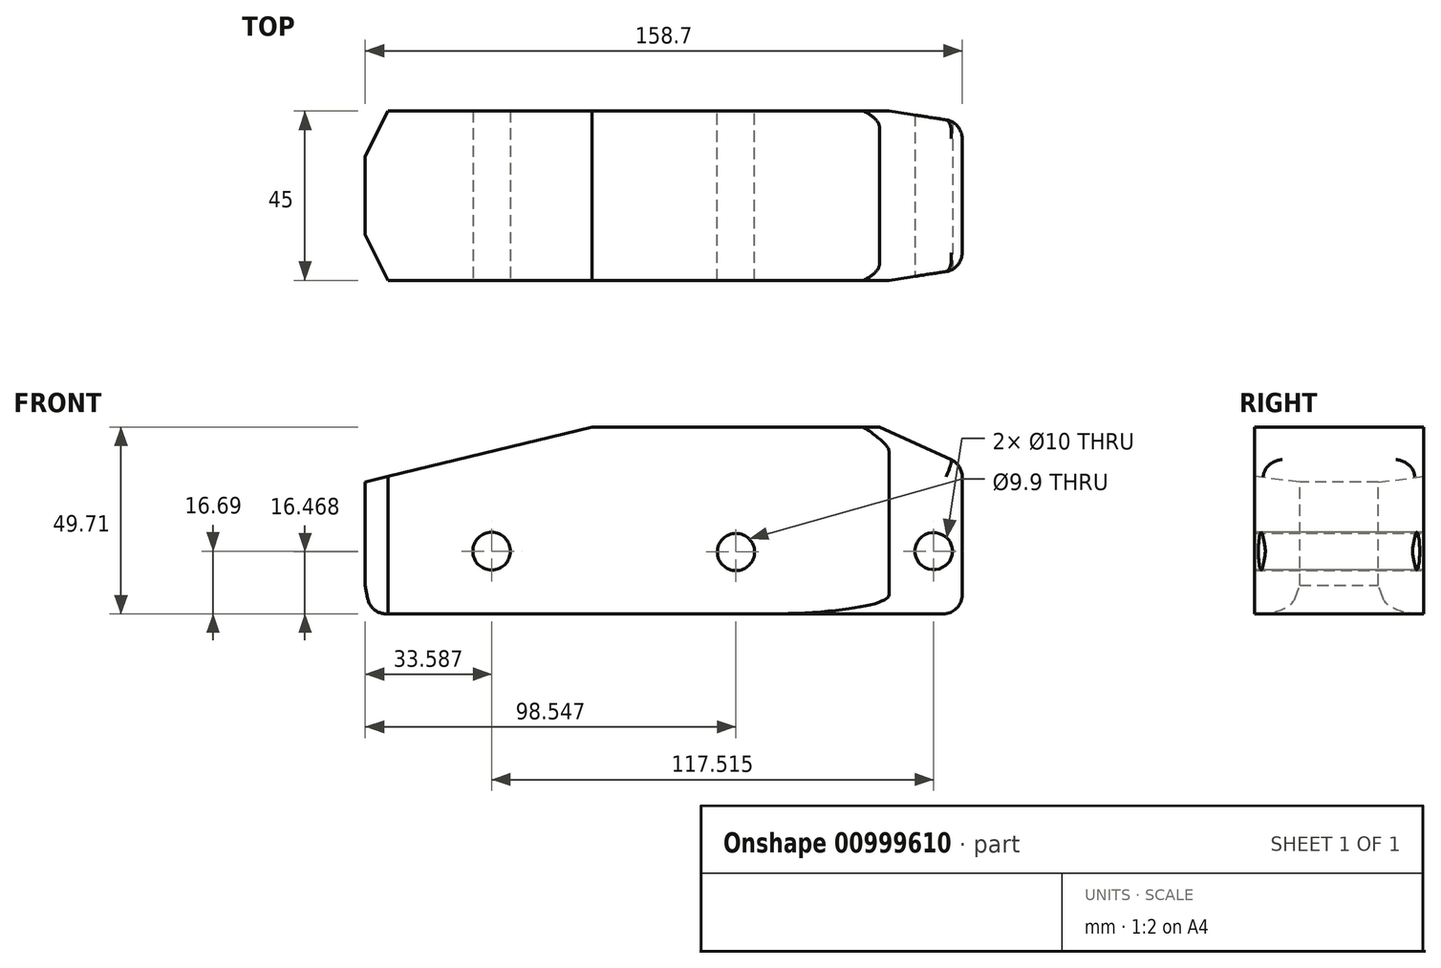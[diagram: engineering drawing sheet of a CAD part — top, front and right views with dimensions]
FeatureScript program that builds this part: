
annotation { "Feature Type Name" : "Feature", "Feature Type Description" : "" }
export const myFeature = defineFeature(function(context is Context, id is Id, definition is map)
    precondition{}
    {
        {
            var Q0;
            Q0=qCreatedBy(makeId("Front.planeOp"),FACE);
            var sketch = newSketch(context, id + "F0", { "sketchPlane" : qUnion([Q0])});
            skLineSegment(sketch, "E0.top", {"start": v(0, -49.7) * mm, "end": v(-135.3, -49.7) * mm});
            skLineSegment(sketch, "E0.left", {"start": v(0, 0) * mm, "end": v(0, -49.7) * mm});
            skLineSegment(sketch, "E1.bottom", {"start": v(0, -49.7) * mm, "end": v(24.63, -49.7) * mm});
            skLineSegment(sketch, "E2", {"start": v(49.26, -22.51) * mm, "end": v(0, 0) * mm});
            skLineSegment(sketch, "E3", {"start": v(24.63, -49.7) * mm, "end": v(49.26, -22.51) * mm});
            skPoint(sketch, "E4.orphan", {"position": v(49.26, -49.7) * mm});
            skLineSegment(sketch, "E5", {"start": v(0, 0) * mm, "end": v(-76.46, 0) * mm});
            skLineSegment(sketch, "E6", {"start": v(-76.46, 0) * mm, "end": v(-141.55, -15.83) * mm});
            skLineSegment(sketch, "E7", {"start": v(-141.55, -15.83) * mm, "end": v(-135.3, -49.7) * mm});
            skSolve(sketch);
        }
        {
            var Q0;
            Q0=makeQuery(id+"F0.imprint","IMPRINT",FACE,{"disambiguationData":[TD([[makeQuery(id+"F0.imprint","IMPRINT",EDGE,{"derivedFrom":sQuery(id+"F0.wireOp",EDGE,"E0.left")}),1.0]])]});
            var Q1;
            Q1=makeQuery(id+"F0.imprint","IMPRINT",FACE,{"disambiguationData":[TD([[makeQuery(id+"F0.imprint","IMPRINT",EDGE,{"derivedFrom":sQuery(id+"F0.wireOp",EDGE,"E0.top")}),-1.0]])]});
            extrude(context, id + "F1", {"entities" : qUnion([Q0, Q1]), "endBound" : BoundingType.SYMMETRIC, "depth" : 45 * mm, "offsetDistance" : 25.4 * mm});
        }
        {
            var Q0;
            Q0=qCreatedBy(makeId("Top.planeOp"),FACE);
            var sketch = newSketch(context, id + "F2", { "sketchPlane" : qUnion([Q0])});
            skLineSegment(sketch, "E8", {"start": v(0, 22.88) * mm, "end": v(24.46, 19.14) * mm});
            skLineSegment(sketch, "E9", {"start": v(24.46, 19.14) * mm, "end": v(42.3, 8.78) * mm});
            skLineSegment(sketch, "E10", {"start": v(42.3, 8.78) * mm, "end": v(46.62, 0) * mm});
            skLineSegment(sketch, "E11.MirrorCS", {"start": v(24.46, -19.14) * mm, "end": v(42.3, -8.78) * mm});
            skLineSegment(sketch, "E12.MirrorCS", {"start": v(0, -22.88) * mm, "end": v(24.46, -19.14) * mm});
            skLineSegment(sketch, "E13.MirrorCS", {"start": v(42.3, -8.78) * mm, "end": v(46.62, 0) * mm});
            skLineSegment(sketch, "E14.bottom", {"start": v(0, 54.83) * mm, "end": v(75.1, 54.83) * mm});
            skLineSegment(sketch, "E14.top", {"start": v(0, -56.55) * mm, "end": v(75.1, -56.55) * mm});
            skLineSegment(sketch, "E14.left", {"start": v(0, 54.83) * mm, "end": v(0, -56.55) * mm});
            skLineSegment(sketch, "E14.right", {"start": v(75.1, 54.83) * mm, "end": v(75.1, -56.55) * mm});
            skLineSegment(sketch, "E15", {"start": v(-130.67, -22.5) * mm, "end": v(-136.72, -10.41) * mm});
            skLineSegment(sketch, "E16", {"start": v(-136.72, -10.41) * mm, "end": v(-136.72, 0) * mm});
            skLineSegment(sketch, "E17.MirrorCS", {"start": v(-130.67, 22.5) * mm, "end": v(-136.72, 10.41) * mm});
            skLineSegment(sketch, "E18.MirrorCS", {"start": v(-136.72, 10.41) * mm, "end": v(-136.72, 0) * mm});
            skLineSegment(sketch, "E19.bottom", {"start": v(-125.78, -39.29) * mm, "end": v(-192.55, -39.29) * mm});
            skLineSegment(sketch, "E19.top", {"start": v(-125.78, 53.96) * mm, "end": v(-192.55, 53.96) * mm});
            skLineSegment(sketch, "E19.left", {"start": v(-125.78, -39.29) * mm, "end": v(-125.78, 53.96) * mm});
            skLineSegment(sketch, "E19.right", {"start": v(-192.55, -39.29) * mm, "end": v(-192.55, 53.96) * mm});
            skLineSegment(sketch, "E20", {"start": v(-130.67, 22.5) * mm, "end": v(-125.78, 22.5) * mm});
            skLineSegment(sketch, "E21", {"start": v(-125.78, 22.5) * mm, "end": v(-130.67, -22.5) * mm});
            skLineSegment(sketch, "E22", {"start": v(-130.67, -22.5) * mm, "end": v(-125.78, -23.03) * mm});
            skSolve(sketch);
        }
        {
            var Q0;
            {var subQ3=sQuery(id+"F2.wireOp",EDGE,"E8");Q0=makeQuery(id+"F2.imprint","IMPRINT",FACE,{"disambiguationData":[TD([[makeQuery(id+"F2.imprint","IMPRINT",EDGE,{"derivedFrom":subQ3}),1.0]])]});}
            extrude(context, id + "F3", {"entities" : qUnion([Q0]), "operationType" : NewBodyOperationType.REMOVE, "oppositeDirection" : true, "depth" : 1016 * mm, "offsetDistance" : 25.4 * mm});
        }
        {
            var Q0;
            Q0=makeQuery(id+"F3.boolean.opBoolean","INTERSECT",EDGE,{"derivedFrom":[makeQuery(id+"F1.opExtrude","SWEPT_FACE",FACE,{"disambiguationData":[OSD([sQuery(id+"F0.wireOp",EDGE,"E2")])]}),makeQuery(id+"F3.opExtrude","SWEPT_FACE",FACE,{"disambiguationData":[OSD([sQuery(id+"F2.wireOp",EDGE,"E12.MirrorCS")])]})]});
            var Q1;
            Q1=makeQuery(id+"F3.boolean.opBoolean","INTERSECT",EDGE,{"derivedFrom":[makeQuery(id+"F1.opExtrude","SWEPT_FACE",FACE,{"disambiguationData":[OSD([sQuery(id+"F0.wireOp",EDGE,"E2")])]}),makeQuery(id+"F3.opExtrude","SWEPT_FACE",FACE,{"disambiguationData":[OSD([sQuery(id+"F2.wireOp",EDGE,"E11.MirrorCS")])]})]});
            var Q2;
            Q2=makeQuery(id+"F3.boolean.opBoolean","INTERSECT",EDGE,{"derivedFrom":[makeQuery(id+"F1.opExtrude","SWEPT_FACE",FACE,{"disambiguationData":[OSD([sQuery(id+"F0.wireOp",EDGE,"E3")])]}),makeQuery(id+"F3.opExtrude","SWEPT_FACE",FACE,{"disambiguationData":[OSD([sQuery(id+"F2.wireOp",EDGE,"E11.MirrorCS")])]})]});
            var Q3;
            Q3=makeQuery(id+"F3.boolean.opBoolean","INTERSECT",EDGE,{"derivedFrom":[makeQuery(id+"F1.opExtrude","SWEPT_FACE",FACE,{"disambiguationData":[OSD([sQuery(id+"F0.wireOp",EDGE,"E0.top"),sQuery(id+"F0.wireOp",EDGE,"E1.bottom")])]}),makeQuery(id+"F3.opExtrude","SWEPT_FACE",FACE,{"disambiguationData":[OSD([sQuery(id+"F2.wireOp",EDGE,"E12.MirrorCS")])]})]});
            var Q4;
            Q4=makeQuery(id+"F3.boolean.opBoolean","INTERSECT",EDGE,{"derivedFrom":[makeQuery(id+"F1.opExtrude","SWEPT_FACE",FACE,{"disambiguationData":[OSD([sQuery(id+"F0.wireOp",EDGE,"E2")])]}),makeQuery(id+"F3.opExtrude","SWEPT_FACE",FACE,{"disambiguationData":[OSD([sQuery(id+"F2.wireOp",EDGE,"E9")])]})]});
            var Q5;
            Q5=makeQuery(id+"F3.boolean.opBoolean","INTERSECT",EDGE,{"derivedFrom":[makeQuery(id+"F1.opExtrude","SWEPT_FACE",FACE,{"disambiguationData":[OSD([sQuery(id+"F0.wireOp",EDGE,"E2")])]}),makeQuery(id+"F3.opExtrude","SWEPT_FACE",FACE,{"disambiguationData":[OSD([sQuery(id+"F2.wireOp",EDGE,"E8")])]})]});
            var Q6;
            Q6=makeQuery(id+"F3.boolean.opBoolean","INTERSECT",EDGE,{"derivedFrom":[makeQuery(id+"F1.opExtrude","SWEPT_FACE",FACE,{"disambiguationData":[OSD([sQuery(id+"F0.wireOp",EDGE,"E3")])]}),makeQuery(id+"F3.opExtrude","SWEPT_FACE",FACE,{"disambiguationData":[OSD([sQuery(id+"F2.wireOp",EDGE,"E9")])]})]});
            var Q7;
            Q7=makeQuery(id+"F3.boolean.opBoolean","INTERSECT",EDGE,{"derivedFrom":[makeQuery(id+"F1.opExtrude","SWEPT_FACE",FACE,{"disambiguationData":[OSD([sQuery(id+"F0.wireOp",EDGE,"E0.top"),sQuery(id+"F0.wireOp",EDGE,"E1.bottom")])]}),makeQuery(id+"F3.opExtrude","SWEPT_FACE",FACE,{"disambiguationData":[OSD([sQuery(id+"F2.wireOp",EDGE,"E8")])]})]});
            fillet(context, id + "F4", {"entities" : qUnion([Q0, Q1, Q2, Q3, Q4, Q5, Q6, Q7]), "radius" : 5.08 * mm, "tangentPropagation" : true, "allowEdgeOverflow" : false});
        }
        {
            var Q0;
            Q0=qCreatedBy(makeId("Front.planeOp"),FACE);
            var sketch = newSketch(context, id + "F5", { "sketchPlane" : qUnion([Q0])});
            skCircle(sketch, "E23", {"center": v(14.38, -33.02) * mm, "radius": 5 * mm});
            skCircle(sketch, "E24", {"center": v(-103.13, -33.02) * mm, "radius": 5 * mm});
            skSolve(sketch);
        }
        {
            var Q0;
            Q0=makeQuery(id+"F2.imprint","IMPRINT",FACE,{"disambiguationData":[TD([[makeQuery(id+"F2.imprint","IMPRINT",EDGE,{"derivedFrom":sQuery(id+"F2.wireOp",EDGE,"E15")}),1.0]])]});
            extrude(context, id + "F6", {"entities" : qUnion([Q0]), "operationType" : NewBodyOperationType.REMOVE, "oppositeDirection" : true, "depth" : 101.6 * mm, "offsetDistance" : 25.4 * mm});
        }
        {
            var Q0;
            Q0=makeQuery(id+"F1.opExtrude","SWEPT_EDGE",EDGE,{"disambiguationData":[OSD([sQuery(id+"F0.wireOp",EDGE,"E0.top"),sQuery(id+"F0.wireOp",EDGE,"E7")])]});
            fillet(context, id + "F7", {"entities" : qUnion([Q0]), "radius" : 5.08 * mm, "tangentPropagation" : true, "allowEdgeOverflow" : false});
        }
        {
            var Q0;
            Q0=makeQuery(id+"F5.imprint","IMPRINT",FACE,{"disambiguationData":[TD([[makeQuery(id+"F5.imprint","IMPRINT",EDGE,{"derivedFrom":sQuery(id+"F5.wireOp",EDGE,"E24")}),1.0]])]});
            var Q1;
            Q1=makeQuery(id+"F5.imprint","IMPRINT",FACE,{"disambiguationData":[TD([[makeQuery(id+"F5.imprint","IMPRINT",EDGE,{"derivedFrom":sQuery(id+"F5.wireOp",EDGE,"E23")}),1.0]])]});
            extrude(context, id + "F8", {"entities" : qUnion([Q0, Q1]), "operationType" : NewBodyOperationType.REMOVE, "endBound" : BoundingType.SYMMETRIC, "oppositeDirection" : true, "depth" : 50.8 * mm, "offsetDistance" : 25.4 * mm});
        }
        {
            var Q0;
            Q0=makeQuery(id+"F1.opExtrude","CAP_FACE",FACE,{"disambiguationData":[OSD([sQuery(id+"F0.wireOp",EDGE,"E0.top"),sQuery(id+"F0.wireOp",EDGE,"E1.bottom"),sQuery(id+"F0.wireOp",EDGE,"E2"),sQuery(id+"F0.wireOp",EDGE,"E3"),sQuery(id+"F0.wireOp",EDGE,"E5"),sQuery(id+"F0.wireOp",EDGE,"E6"),sQuery(id+"F0.wireOp",EDGE,"E7")])],"isStart":true});
            var sketch = newSketch(context, id + "F9", { "sketchPlane" : qUnion([Q0])});
            skCircle(sketch, "E25", {"center": v(38.17, -33.24) * mm, "radius": 4.95 * mm});
            skSolve(sketch);
        }
        {
            var Q0;
            Q0=makeQuery(id+"F9.imprint","IMPRINT",FACE,{"disambiguationData":[TD([[makeQuery(id+"F9.imprint","IMPRINT",EDGE,{"derivedFrom":sQuery(id+"F9.wireOp",EDGE,"E25")}),1.0]])]});
            var sketch = newSketch(context, id + "F10", { "sketchPlane" : qUnion([Q0])});
            skSolve(sketch);
        }
        {
            var Q0;
            Q0=makeQuery(id+"F10.imprint","IMPRINT",FACE,{"disambiguationData":[TD([[makeQuery(id+"F10.imprint","IMPRINT",EDGE,{"derivedFrom":makeQuery(id+"F9.imprint","IMPRINT",EDGE,{"derivedFrom":sQuery(id+"F9.wireOp",EDGE,"E25")})}),1.0]])]});
            extrude(context, id + "F11", {"entities" : qUnion([Q0]), "operationType" : NewBodyOperationType.REMOVE, "oppositeDirection" : true, "depth" : 254 * mm, "offsetDistance" : 25.4 * mm});
        }
        {
            var Q0;
            Q0=qCreatedBy(makeId("Front.planeOp"),FACE);
            var sketch = newSketch(context, id + "F12", { "sketchPlane" : qUnion([Q0])});
            skLineSegment(sketch, "E26.bottom", {"start": v(21.98, 0) * mm, "end": v(60.26, 0) * mm});
            skLineSegment(sketch, "E26.top", {"start": v(21.98, -64.32) * mm, "end": v(60.26, -64.32) * mm});
            skLineSegment(sketch, "E26.left", {"start": v(21.98, 0) * mm, "end": v(21.98, -64.32) * mm});
            skLineSegment(sketch, "E26.right", {"start": v(60.26, 0) * mm, "end": v(60.26, -64.32) * mm});
            skSolve(sketch);
        }
        {
            var Q0;
            Q0=makeQuery(id+"F12.imprint","IMPRINT",FACE,{"disambiguationData":[TD([[makeQuery(id+"F12.imprint","IMPRINT",EDGE,{"derivedFrom":sQuery(id+"F12.wireOp",EDGE,"E26.bottom")}),-1.0]])]});
            extrude(context, id + "F13", {"entities" : qUnion([Q0]), "operationType" : NewBodyOperationType.REMOVE, "endBound" : BoundingType.SYMMETRIC, "depth" : 50.8 * mm, "offsetDistance" : 25.4 * mm});
        }
        {
            var Q0;
            Q0=makeQuery(id+"F13.boolean.opBoolean","INTERSECT",EDGE,{"derivedFrom":[makeQuery(id+"F1.opExtrude","SWEPT_FACE",FACE,{"disambiguationData":[OSD([sQuery(id+"F0.wireOp",EDGE,"E2")])]}),makeQuery(id+"F13.opExtrude","SWEPT_FACE",FACE,{"disambiguationData":[OSD([sQuery(id+"F12.wireOp",EDGE,"E26.left")])]})]});
            fillet(context, id + "F14", {"entities" : qUnion([Q0]), "radius" : 5.08 * mm, "tangentPropagation" : true, "allowEdgeOverflow" : false});
        }
    });
